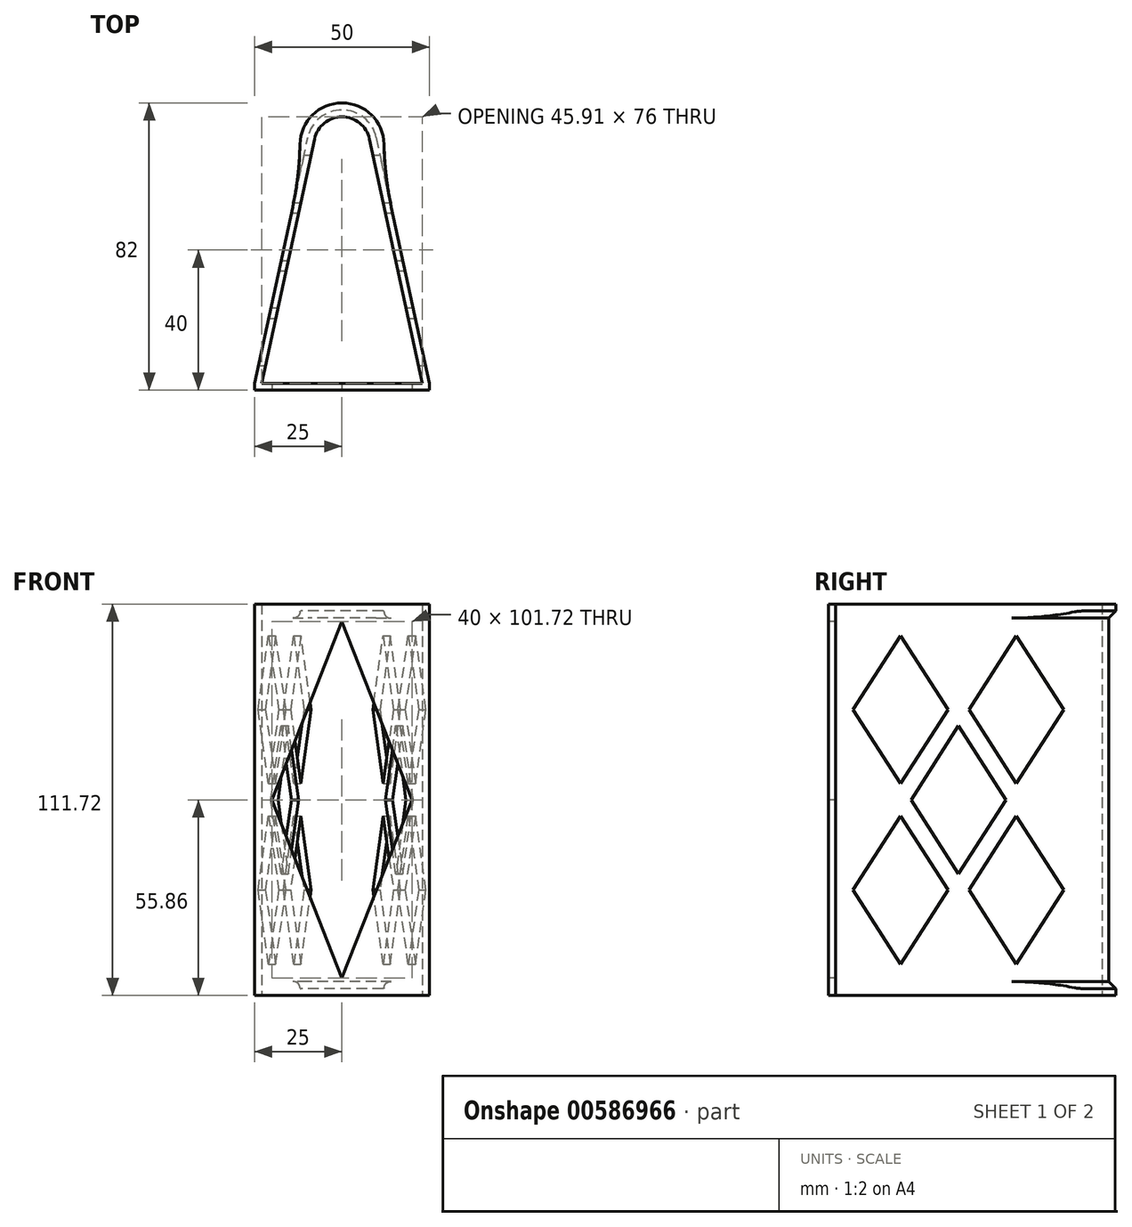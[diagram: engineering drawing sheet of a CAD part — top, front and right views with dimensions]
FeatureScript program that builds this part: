
annotation { "Feature Type Name" : "Feature", "Feature Type Description" : "" }
export const myFeature = defineFeature(function(context is Context, id is Id, definition is map)
    precondition{}
    {
        {
            var Q0;
            Q0=qCreatedBy(makeId("Top.planeOp"),FACE);
            var sketch = newSketch(context, id + "F0", { "sketchPlane" : qUnion([Q0])});
            skArc(sketch, "E0", {"start": v(9.77, 2.12) * mm, "mid": v(0, 10) * mm, "end": v(-9.77, 2.12) * mm});
            skArc(sketch, "E1", {"start": v(7.82, 1.7) * mm, "mid": v(0, 8) * mm, "end": v(-7.82, 1.7) * mm});
            skLineSegment(sketch, "E2", {"start": v(-9.77, 2.12) * mm, "end": v(-25, -68) * mm});
            skLineSegment(sketch, "E3", {"start": v(-25, -68) * mm, "end": v(-25, -70) * mm});
            skLineSegment(sketch, "E4", {"start": v(-25, -70) * mm, "end": v(0, -70) * mm});
            skLineSegment(sketch, "E5", {"start": v(0, -68) * mm, "end": v(-22.95, -68) * mm});
            skLineSegment(sketch, "E6", {"start": v(-22.95, -68) * mm, "end": v(-7.82, 1.7) * mm});
            skLineSegment(sketch, "E7.MirrorCS", {"start": v(25, -68) * mm, "end": v(25, -70) * mm});
            skLineSegment(sketch, "E8.MirrorCS", {"start": v(25, -70) * mm, "end": v(0, -70) * mm});
            skLineSegment(sketch, "E9.MirrorCS", {"start": v(0, -68) * mm, "end": v(22.95, -68) * mm});
            skLineSegment(sketch, "E10.MirrorCS", {"start": v(22.95, -68) * mm, "end": v(7.82, 1.7) * mm});
            skLineSegment(sketch, "E11.MirrorCS", {"start": v(9.77, 2.12) * mm, "end": v(25, -68) * mm});
            skArc(sketch, "E12", {"start": v(11.18, -4.36) * mm, "mid": v(0, 12) * mm, "end": v(-11.18, -4.36) * mm});
            skSolve(sketch);
        }
        {
            var Q0;
            Q0=makeQuery(id+"F0.imprint","IMPRINT",FACE,{"disambiguationData":[TD([[makeQuery(id+"F0.imprint","IMPRINT",EDGE,{"derivedFrom":sQuery(id+"F0.wireOp",EDGE,"E0")}),1.0]])]});
            var Q1;
            Q1=makeQuery(id+"F0.imprint","IMPRINT",FACE,{"disambiguationData":[TD([[makeQuery(id+"F0.imprint","IMPRINT",EDGE,{"derivedFrom":sQuery(id+"F0.wireOp",EDGE,"E0")}),-1.0]])]});
            extrude(context, id + "F1", {"entities" : qUnion([Q0, Q1]), "endBound" : BoundingType.SYMMETRIC, "depth" : 111.72 * mm, "offsetDistance" : 25 * mm});
        }
        {
            var Q0;
            Q0=makeQuery(id+"F0.imprint","IMPRINT",FACE,{"disambiguationData":[TD([[makeQuery(id+"F0.imprint","IMPRINT",EDGE,{"derivedFrom":sQuery(id+"F0.wireOp",EDGE,"E0")}),-1.0]])]});
            extrude(context, id + "F2", {"entities" : qUnion([Q0]), "operationType" : NewBodyOperationType.REMOVE, "endBound" : BoundingType.SYMMETRIC, "oppositeDirection" : true, "depth" : (96 + 11.72) * mm, "offsetDistance" : 25 * mm});
        }
        {
            var Q0;
            {var subQ0=sQuery(id+"F0.wireOp",EDGE,"E12");var subQ1=sQuery(id+"F0.wireOp",EDGE,"E2");var subQ2=sQuery(id+"F0.wireOp",EDGE,"E11.MirrorCS");Q0=makeQuery(id+"F2.boolean.opBoolean","SPLIT",EDGE,{"disambiguationData":[TD([makeQuery(id+"F2.opExtrude","CAP_FACE",FACE,{"disambiguationData":[OSD([sQuery(id+"F0.wireOp",EDGE,"E0"),subQ1,subQ2,subQ0])],"isStart":true})])],"derivedFrom":makeQuery(id+"F1.opExtrude","SWEPT_EDGE",EDGE,{"disambiguationData":[OSD([subQ1,subQ0])]})});}
            var Q1;
            {var subQ0=sQuery(id+"F0.wireOp",EDGE,"E12");var subQ1=sQuery(id+"F0.wireOp",EDGE,"E11.MirrorCS");var subQ2=sQuery(id+"F0.wireOp",EDGE,"E2");Q1=makeQuery(id+"F2.boolean.opBoolean","SPLIT",EDGE,{"disambiguationData":[TD([makeQuery(id+"F2.opExtrude","CAP_FACE",FACE,{"disambiguationData":[OSD([sQuery(id+"F0.wireOp",EDGE,"E0"),subQ2,subQ1,subQ0])],"isStart":true})])],"derivedFrom":makeQuery(id+"F1.opExtrude","SWEPT_EDGE",EDGE,{"disambiguationData":[OSD([subQ1,subQ0])]})});}
            var Q2;
            {var subQ0=sQuery(id+"F0.wireOp",EDGE,"E12");var subQ1=sQuery(id+"F0.wireOp",EDGE,"E11.MirrorCS");var subQ2=sQuery(id+"F0.wireOp",EDGE,"E2");Q2=makeQuery(id+"F2.boolean.opBoolean","SPLIT",EDGE,{"disambiguationData":[TD([makeQuery(id+"F2.opExtrude","CAP_FACE",FACE,{"disambiguationData":[OSD([sQuery(id+"F0.wireOp",EDGE,"E0"),subQ2,subQ1,subQ0])],"isStart":false})])],"derivedFrom":makeQuery(id+"F1.opExtrude","SWEPT_EDGE",EDGE,{"disambiguationData":[OSD([subQ1,subQ0])]})});}
            var Q3;
            {var subQ0=sQuery(id+"F0.wireOp",EDGE,"E12");var subQ1=sQuery(id+"F0.wireOp",EDGE,"E11.MirrorCS");var subQ2=sQuery(id+"F0.wireOp",EDGE,"E2");Q3=makeQuery(id+"F2.boolean.opBoolean","SPLIT",EDGE,{"disambiguationData":[TD([makeQuery(id+"F2.opExtrude","CAP_FACE",FACE,{"disambiguationData":[OSD([sQuery(id+"F0.wireOp",EDGE,"E0"),subQ2,subQ1,subQ0])],"isStart":false})])],"derivedFrom":makeQuery(id+"F1.opExtrude","SWEPT_EDGE",EDGE,{"disambiguationData":[OSD([subQ2,subQ0])]})});}
            fillet(context, id + "F3", {"entities" : qUnion([Q0, Q1, Q2, Q3]), "tangentPropagation" : true, "radius" : 92.2 * mm, "defaultsChanged" : true, "vertexSettings" : [], "allowEdgeOverflow" : false});
        }
        {
            var Q0;
            Q0=makeQuery(id+"F2.boolean.opBoolean","COPY",EDGE,{"derivedFrom":makeQuery(id+"F2.opExtrude","CAP_EDGE",EDGE,{"disambiguationData":[OSD([sQuery(id+"F0.wireOp",EDGE,"E0")])],"isStart":false})});
            var Q1;
            Q1=makeQuery(id+"F2.boolean.opBoolean","COPY",EDGE,{"derivedFrom":makeQuery(id+"F2.opExtrude","CAP_EDGE",EDGE,{"disambiguationData":[OSD([sQuery(id+"F0.wireOp",EDGE,"E0")])],"isStart":true})});
            chamfer(context, id + "F4", {"entities" : qUnion([Q0, Q1]), "width" : 2 * mm, "tangentPropagation" : true});
        }
        {
            var Q0;
            Q0=qCreatedBy(makeId("Right.planeOp"),FACE);
            var sketch = newSketch(context, id + "F5", { "sketchPlane" : qUnion([Q0])});
            skLineSegment(sketch, "E13", {"start": v(-49.45, -4.63) * mm, "end": v(-35.9, -25.75) * mm});
            skLineSegment(sketch, "E14", {"start": v(-35.9, -25.75) * mm, "end": v(-49.45, -46.86) * mm});
            skLineSegment(sketch, "E15", {"start": v(-49.45, -46.86) * mm, "end": v(-63, -25.75) * mm});
            skLineSegment(sketch, "E16", {"start": v(-63, -25.75) * mm, "end": v(-49.45, -4.63) * mm});
            skLineSegment(sketch, "E17.1.0.0", {"start": v(-32.94, -72.6) * mm, "end": v(-46.48, -51.5) * mm});
            skLineSegment(sketch, "E17.1.0.1", {"start": v(-32.94, -30.38) * mm, "end": v(-19.4, -51.5) * mm});
            skLineSegment(sketch, "E17.1.0.2", {"start": v(-19.4, -51.5) * mm, "end": v(-32.94, -72.6) * mm});
            skLineSegment(sketch, "E17.1.0.3", {"start": v(-46.48, -51.5) * mm, "end": v(-32.94, -30.38) * mm});
            skLineSegment(sketch, "E17.direction1", {"start": v(-49.45, -46.86) * mm, "end": v(-32.94, -72.6) * mm, "construction": true});
            skLineSegment(sketch, "E18.0.2.0", {"start": v(-16.42, -98.35) * mm, "end": v(-29.97, -77.24) * mm});
            skLineSegment(sketch, "E18.3.2.0", {"start": v(-16.42, -56.12) * mm, "end": v(-2.88, -77.24) * mm});
            skLineSegment(sketch, "E18.6.2.0", {"start": v(-2.88, -77.24) * mm, "end": v(-16.42, -98.35) * mm});
            skLineSegment(sketch, "E18.9.2.0", {"start": v(-29.97, -77.24) * mm, "end": v(-16.42, -56.12) * mm});
            skLineSegment(sketch, "E19.0.1.0", {"start": v(-49.45, 4.63) * mm, "end": v(-63, 25.75) * mm});
            skLineSegment(sketch, "E19.0.1.1", {"start": v(-29.97, -25.75) * mm, "end": v(-16.42, -4.63) * mm});
            skLineSegment(sketch, "E19.0.1.2", {"start": v(-19.4, 0) * mm, "end": v(-32.94, -21.11) * mm});
            skLineSegment(sketch, "E19.0.1.3", {"start": v(-16.42, -4.63) * mm, "end": v(-2.88, -25.75) * mm});
            skLineSegment(sketch, "E19.0.1.4", {"start": v(-16.42, -46.86) * mm, "end": v(-29.97, -25.75) * mm});
            skLineSegment(sketch, "E19.0.1.5", {"start": v(-49.45, 4.63) * mm, "end": v(-32.94, -21.11) * mm, "construction": true});
            skLineSegment(sketch, "E19.0.1.6", {"start": v(-32.94, 21.11) * mm, "end": v(-19.4, 0) * mm});
            skLineSegment(sketch, "E19.0.1.7", {"start": v(-2.88, -25.75) * mm, "end": v(-16.42, -46.86) * mm});
            skLineSegment(sketch, "E19.0.1.8", {"start": v(-49.45, 46.86) * mm, "end": v(-35.9, 25.75) * mm});
            skLineSegment(sketch, "E19.0.1.9", {"start": v(-35.9, 25.75) * mm, "end": v(-49.45, 4.63) * mm});
            skLineSegment(sketch, "E19.0.1.10", {"start": v(-46.48, 0) * mm, "end": v(-32.94, 21.11) * mm});
            skLineSegment(sketch, "E19.0.1.11", {"start": v(-63, 25.75) * mm, "end": v(-49.45, 46.86) * mm});
            skLineSegment(sketch, "E19.0.1.12", {"start": v(-32.94, -21.11) * mm, "end": v(-46.48, 0) * mm});
            skLineSegment(sketch, "E19.0.2.0", {"start": v(-49.45, 56.12) * mm, "end": v(-63, 77.24) * mm});
            skLineSegment(sketch, "E19.0.2.1", {"start": v(-29.97, 25.75) * mm, "end": v(-16.42, 46.86) * mm});
            skLineSegment(sketch, "E19.0.2.2", {"start": v(-19.4, 51.5) * mm, "end": v(-32.94, 30.38) * mm});
            skLineSegment(sketch, "E19.0.2.3", {"start": v(-16.42, 46.86) * mm, "end": v(-2.88, 25.75) * mm});
            skLineSegment(sketch, "E19.0.2.4", {"start": v(-16.42, 4.63) * mm, "end": v(-29.97, 25.75) * mm});
            skLineSegment(sketch, "E19.0.2.5", {"start": v(-49.45, 56.12) * mm, "end": v(-32.94, 30.38) * mm, "construction": true});
            skLineSegment(sketch, "E19.0.2.6", {"start": v(-32.94, 72.6) * mm, "end": v(-19.4, 51.5) * mm});
            skLineSegment(sketch, "E19.0.2.7", {"start": v(-2.88, 25.75) * mm, "end": v(-16.42, 4.63) * mm});
            skLineSegment(sketch, "E19.0.2.8", {"start": v(-49.45, 98.35) * mm, "end": v(-35.9, 77.24) * mm});
            skLineSegment(sketch, "E19.0.2.9", {"start": v(-35.9, 77.24) * mm, "end": v(-49.45, 56.12) * mm});
            skLineSegment(sketch, "E19.0.2.10", {"start": v(-46.48, 51.5) * mm, "end": v(-32.94, 72.6) * mm});
            skLineSegment(sketch, "E19.0.2.11", {"start": v(-63, 77.24) * mm, "end": v(-49.45, 98.35) * mm});
            skLineSegment(sketch, "E19.0.2.12", {"start": v(-32.94, 30.38) * mm, "end": v(-46.48, 51.5) * mm});
            skLineSegment(sketch, "E19.0.3.0", {"start": v(-49.45, 107.61) * mm, "end": v(-63, 128.73) * mm});
            skLineSegment(sketch, "E19.0.3.1", {"start": v(-29.97, 77.24) * mm, "end": v(-16.42, 98.35) * mm});
            skLineSegment(sketch, "E19.0.3.2", {"start": v(-19.4, 102.98) * mm, "end": v(-32.94, 81.87) * mm});
            skLineSegment(sketch, "E19.0.3.3", {"start": v(-16.42, 98.35) * mm, "end": v(-2.88, 77.24) * mm});
            skLineSegment(sketch, "E19.0.3.4", {"start": v(-16.42, 56.12) * mm, "end": v(-29.97, 77.24) * mm});
            skLineSegment(sketch, "E19.0.3.5", {"start": v(-49.45, 107.61) * mm, "end": v(-32.94, 81.87) * mm, "construction": true});
            skLineSegment(sketch, "E19.0.3.6", {"start": v(-32.94, 124.1) * mm, "end": v(-19.4, 102.98) * mm});
            skLineSegment(sketch, "E19.0.3.7", {"start": v(-2.88, 77.24) * mm, "end": v(-16.42, 56.12) * mm});
            skLineSegment(sketch, "E19.0.3.8", {"start": v(-49.45, 149.84) * mm, "end": v(-35.9, 128.73) * mm});
            skLineSegment(sketch, "E19.0.3.9", {"start": v(-35.9, 128.73) * mm, "end": v(-49.45, 107.61) * mm});
            skLineSegment(sketch, "E19.0.3.10", {"start": v(-46.48, 102.98) * mm, "end": v(-32.94, 124.1) * mm});
            skLineSegment(sketch, "E19.0.3.11", {"start": v(-63, 128.73) * mm, "end": v(-49.45, 149.84) * mm});
            skLineSegment(sketch, "E19.0.3.12", {"start": v(-32.94, 81.87) * mm, "end": v(-46.48, 102.98) * mm});
            skLineSegment(sketch, "E19.direction1", {"start": v(-16.42, -98.35) * mm, "end": v(1.3, -98.35) * mm, "construction": true});
            skLineSegment(sketch, "E19.direction2", {"start": v(-16.42, -98.35) * mm, "end": v(-16.42, -46.86) * mm, "construction": true});
            skSolve(sketch);
        }
        {
            var Q0;
            Q0=makeQuery(id+"F5.imprint","IMPRINT",FACE,{"disambiguationData":[TD([[makeQuery(id+"F5.imprint","IMPRINT",EDGE,{"derivedFrom":sQuery(id+"F5.wireOp",EDGE,"E19.0.1.1")}),-1.0]])]});
            var Q1;
            Q1=makeQuery(id+"F5.imprint","IMPRINT",FACE,{"disambiguationData":[TD([[makeQuery(id+"F5.imprint","IMPRINT",EDGE,{"derivedFrom":sQuery(id+"F5.wireOp",EDGE,"E13")}),-1.0]])]});
            var Q2;
            Q2=makeQuery(id+"F5.imprint","IMPRINT",FACE,{"disambiguationData":[TD([[makeQuery(id+"F5.imprint","IMPRINT",EDGE,{"derivedFrom":sQuery(id+"F5.wireOp",EDGE,"E19.0.1.2")}),-1.0]])]});
            var Q3;
            Q3=makeQuery(id+"F5.imprint","IMPRINT",FACE,{"disambiguationData":[TD([[makeQuery(id+"F5.imprint","IMPRINT",EDGE,{"derivedFrom":sQuery(id+"F5.wireOp",EDGE,"E19.0.2.1")}),-1.0]])]});
            var Q4;
            Q4=makeQuery(id+"F5.imprint","IMPRINT",FACE,{"disambiguationData":[TD([[makeQuery(id+"F5.imprint","IMPRINT",EDGE,{"derivedFrom":sQuery(id+"F5.wireOp",EDGE,"E19.0.1.0")}),-1.0]])]});
            var Q5;
            Q5=makeQuery(id+"F5.imprint","IMPRINT",FACE,{"disambiguationData":[TD([[makeQuery(id+"F5.imprint","IMPRINT",EDGE,{"derivedFrom":sQuery(id+"F5.wireOp",EDGE,"E19.0.2.0")}),-1.0]])]});
            var Q6;
            Q6=makeQuery(id+"F5.imprint","IMPRINT",FACE,{"disambiguationData":[TD([[makeQuery(id+"F5.imprint","IMPRINT",EDGE,{"derivedFrom":sQuery(id+"F5.wireOp",EDGE,"E19.0.3.1")}),-1.0]])]});
            extrude(context, id + "F6", {"entities" : qUnion([Q0, Q1, Q2, Q3, Q4, Q5, Q6]), "operationType" : NewBodyOperationType.REMOVE, "endBound" : BoundingType.SYMMETRIC, "oppositeDirection" : true, "depth" : 66.6 * mm, "offsetDistance" : 25 * mm});
        }
        {
            var Q0;
            Q0=makeQuery(id+"F1.opExtrude","SWEPT_FACE",FACE,{"disambiguationData":[OSD([sQuery(id+"F0.wireOp",EDGE,"E4"),sQuery(id+"F0.wireOp",EDGE,"E8.MirrorCS")])]});
            var sketch = newSketch(context, id + "F7", { "sketchPlane" : qUnion([Q0])});
            skLineSegment(sketch, "E20", {"start": v(0, -50.86) * mm, "end": v(20, 0) * mm});
            skPoint(sketch, "E20.startSnap0", {"position": v(0, -55.86) * mm});
            skPoint(sketch, "E20.endSnap0", {"position": v(25, 0) * mm});
            skLineSegment(sketch, "E21", {"start": v(20, 0) * mm, "end": v(0, 50.86) * mm});
            skPoint(sketch, "E21.endSnap0", {"position": v(0, 55.86) * mm});
            skLineSegment(sketch, "E22", {"start": v(0, 50.86) * mm, "end": v(-20, 0) * mm});
            skPoint(sketch, "E22.endSnap0", {"position": v(-25, 0) * mm});
            skLineSegment(sketch, "E23", {"start": v(-20, 0) * mm, "end": v(0, -50.86) * mm});
            skSolve(sketch);
        }
        {
            var Q0;
            Q0=makeQuery(id+"F7.imprint","IMPRINT",FACE,{"disambiguationData":[TD([[makeQuery(id+"F7.imprint","IMPRINT",EDGE,{"derivedFrom":sQuery(id+"F7.wireOp",EDGE,"E20")}),1.0]])]});
            extrude(context, id + "F8", {"entities" : qUnion([Q0]), "operationType" : NewBodyOperationType.REMOVE, "endBound" : BoundingType.UP_TO_NEXT, "oppositeDirection" : true, "depth" : 25 * mm, "offsetDistance" : 25 * mm});
        }
    });
